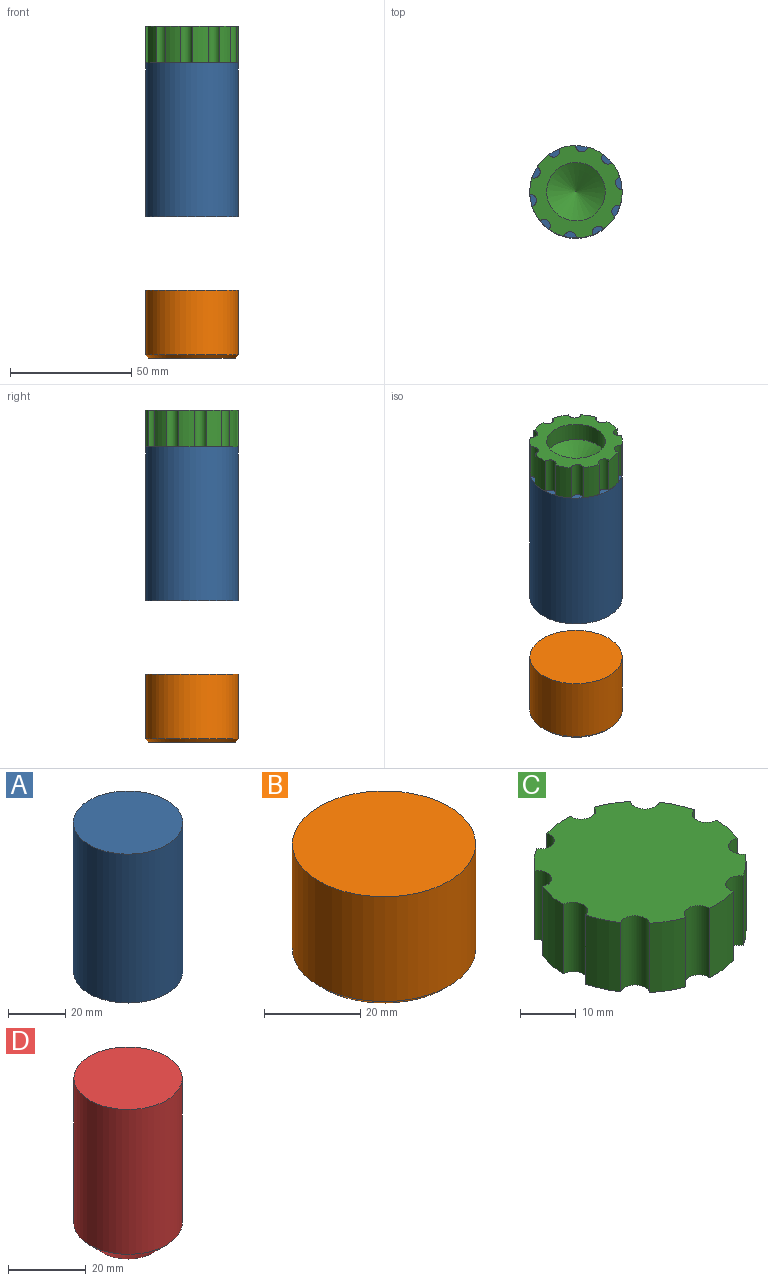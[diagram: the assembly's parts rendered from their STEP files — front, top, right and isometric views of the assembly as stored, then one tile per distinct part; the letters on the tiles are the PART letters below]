
ASSEMBLY  parts=4 mates=3
PART A: 5 faces, bbox 38.1x38.1x63.5 mm
  f0: cylinder r=19.05mm len=63.5mm, axis (0,0,-1), area 7600.6mm2, adj f1,f2
  f1: plane 38.1x38.1mm, normal (0,0,1), area 1140.1mm2, adj f0
  f2: plane 38.1x38.1mm, normal (0,0,-1), area 283.8mm2, adj f0,f4
  f3: cone r=0mm half-angle=59deg, axis (0,0,-1), area 999mm2, adj f4
  f4: cylinder r=16.51mm len=50.8mm, axis (0,0,-1), area 5269.8mm2, adj f2,f3
PART B: 7 faces, bbox 38.1x38.1x27.9 mm
  f0: cylinder r=19.05mm len=38.1mm, axis (0,0,-1), area 3192.3mm2, adj f1,f3
  f1: plane 38.1x38.1mm, normal (0,0,1), area 1140.1mm2, adj f0
  f2: plane 35.56x35.56mm, normal (0,0,-1), area 987mm2, adj f3,f6
  f3: cone r=19.05mm half-angle=45deg, axis (0,0,1), area 207.8mm2, adj f0,f2
  f4: cylinder r=1.14mm len=2.29mm, axis (0,0,-1), area 1.8mm2, adj f5,f6
  f5: plane 2.29x2.29mm, normal (0,0,-1), area 4.1mm2, adj f4
  f6: torus R=1.4mm, axis (0,0,1), area 3.1mm2, adj f2,f4
PART C: 24 faces, bbox 38.1x38.1x15.2 mm
  f0: cylinder r=19.05mm len=15.24mm, axis (0,0,-1), area 104.2mm2, adj f9,f11,f22,f23
  f1: cylinder r=19.05mm len=15.24mm, axis (0,0,-1), area 104.2mm2, adj f9,f11,f21,f22
  f2: cylinder r=19.05mm len=15.24mm, axis (0,0,-1), area 104.2mm2, adj f9,f11,f20,f21
  f3: cylinder r=19.05mm len=15.24mm, axis (0,0,-1), area 104.2mm2, adj f9,f11,f19,f20
  f4: cylinder r=19.05mm len=15.24mm, axis (0,0,-1), area 104.2mm2, adj f9,f11,f18,f19
  f5: cylinder r=19.05mm len=15.24mm, axis (0,0,-1), area 104.2mm2, adj f9,f11,f16,f18
  f6: cylinder r=19.05mm len=15.24mm, axis (0,0,-1), area 104.2mm2, adj f9,f11,f14,f17
  f7: cylinder r=19.05mm len=15.24mm, axis (0,0,-1), area 104.2mm2, adj f9,f11,f16,f17
  f8: cylinder r=19.05mm len=15.24mm, axis (0,0,-1), area 104.2mm2, adj f9,f11,f15,f23
  f9: plane 38.1x38.09mm, normal (0,0,-1), area 588.9mm2, adj f0,f1,f2,f3,f4,f5,f6,f7
  f10: cylinder r=19.05mm len=15.24mm, axis (0,0,-1), area 104.2mm2, adj f9,f11,f14,f15
  f11: plane 38.1x38.09mm, normal (0,0,1), area 1046.2mm2, adj f0,f1,f2,f3,f4,f5,f6,f7
  f12: cone r=0mm half-angle=59deg, axis (0,0,-1), area 533.5mm2, adj f13
  f13: cylinder r=12.06mm len=24.13mm, axis (0,0,-1), area 577.6mm2, adj f9,f12
  f14: cylinder r=2.58mm len=15.24mm, axis (0,0,-1), area 113.7mm2, adj f6,f9,f10,f11
  f15: cylinder r=2.58mm len=15.24mm, axis (0,0,-1), area 113.7mm2, adj f8,f9,f10,f11
  f16: cylinder r=2.58mm len=15.24mm, axis (0,0,-1), area 113.7mm2, adj f5,f7,f9,f11
  f17: cylinder r=2.58mm len=15.24mm, axis (0,0,-1), area 113.7mm2, adj f6,f7,f9,f11
  f18: cylinder r=2.58mm len=15.24mm, axis (0,0,-1), area 113.7mm2, adj f4,f5,f9,f11
  f19: cylinder r=2.58mm len=15.24mm, axis (0,0,-1), area 113.7mm2, adj f3,f4,f9,f11
  f20: cylinder r=2.58mm len=15.24mm, axis (0,0,-1), area 113.7mm2, adj f2,f3,f9,f11
  f21: cylinder r=2.58mm len=15.24mm, axis (0,0,-1), area 113.7mm2, adj f1,f2,f9,f11
  f22: cylinder r=2.58mm len=15.24mm, axis (0,0,-1), area 113.7mm2, adj f0,f1,f9,f11
  f23: cylinder r=2.58mm len=15.24mm, axis (0,0,-1), area 113.7mm2, adj f0,f8,f9,f11
PART D: 4 faces, bbox 27.9x27.9x50.8 mm
  f0: cylinder r=13.97mm len=45.72mm, axis (0,0,-1), area 4013.1mm2, adj f1,f3
  f1: plane 27.94x27.94mm, normal (0,0,1), area 613.1mm2, adj f0
  f2: plane 17.78x17.78mm, normal (0,0,-1), area 248.3mm2, adj f3
  f3: cone r=13.97mm half-angle=45deg, axis (0,0,1), area 515.9mm2, adj f0,f2
PLACE A rot(axis=(0,0,-1),69.4deg) t=(-68.98,-116.13,27.78)mm
PLACE B rot(axis=(0,0,-1),69.4deg) t=(-97.26,-40.73,-30.38)mm
PLACE C rot(axis=(-0.45,0.89,0),180deg) t=(-57.12,12.79,106.52)mm
PLACE D rot(axis=(0,0,-1),69.4deg) t=(-153.49,-61.81,28.69)mm
MATE slider B.f0 <-> A.f3  axis (0,0,1) through (-97.26,-40.73,-2.44)mm
MATE revolute C.f0 <-> A.f0  axis (0,0,-1) through (-97.26,-40.73,91.28)mm
MATE slider D.f0 <-> A.f3  axis (0,0,1) through (-97.26,-40.73,79.49)mm
